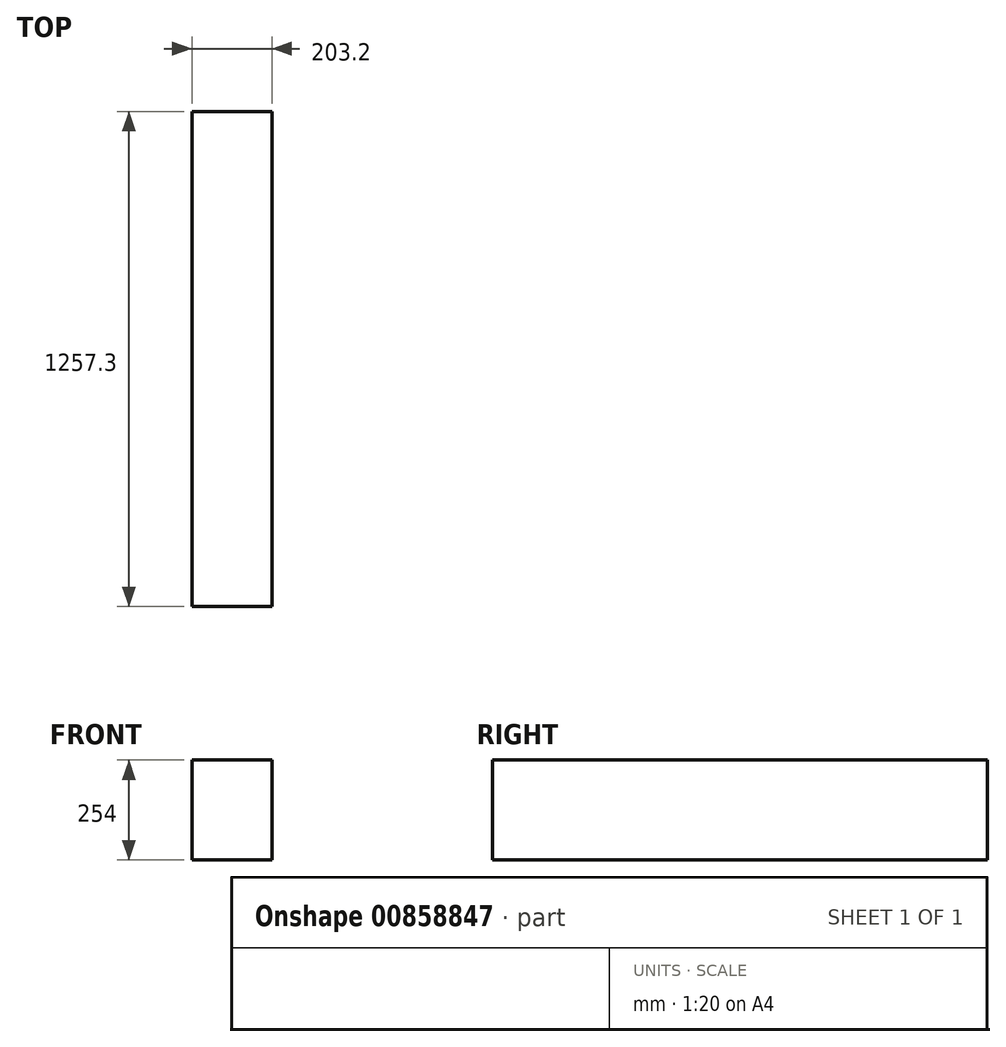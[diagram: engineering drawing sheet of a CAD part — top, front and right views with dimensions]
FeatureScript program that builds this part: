
annotation { "Feature Type Name" : "Feature", "Feature Type Description" : "" }
export const myFeature = defineFeature(function(context is Context, id is Id, definition is map)
    precondition{}
    {
        {
            var Q0;
            Q0=qCreatedBy(makeId("Front.planeOp"),FACE);
            var sketch = newSketch(context, id + "F0", { "sketchPlane" : qUnion([Q0])});
            skLineSegment(sketch, "E0.bottom", {"start": v(-40.1, -27.2) * mm, "end": v(163.1, -27.2) * mm});
            skLineSegment(sketch, "E0.top", {"start": v(-40.1, 226.8) * mm, "end": v(163.1, 226.8) * mm});
            skLineSegment(sketch, "E0.left", {"start": v(-40.1, -27.2) * mm, "end": v(-40.1, 226.8) * mm});
            skLineSegment(sketch, "E0.right", {"start": v(163.1, -27.2) * mm, "end": v(163.1, 226.8) * mm});
            skSolve(sketch);
        }
        {
            var Q0;
            Q0=makeQuery(id+"F0.imprint","IMPRINT",FACE,{"disambiguationData":[TD([[makeQuery(id+"F0.imprint","IMPRINT",EDGE,{"derivedFrom":sQuery(id+"F0.wireOp",EDGE,"E0.bottom")}),1.0]])]});
            extrude(context, id + "F1", {"entities" : qUnion([Q0]), "depth" : 1257.3 * mm, "offsetDistance" : 25.4 * mm});
        }
    });
